# Revit family: Maxlogic sirène,flasheur,Sirène avec flasheur (Haute IP)
name_source: partatom
category: Fire Alarm Devices
units: mm (PartAtom-declared; Revit-internal decimal feet)

## family parameters
Cut with Voids When Loaded = No
Host = Face
Maintain Annotation Orientation = Yes
OmniClass Number = 23.85.30.21
OmniClass Title = Environmental Detection/Registration
Part Type = Normal
Room Calculation Point = No
Round Connector Dimension = Use Diameter
Shared = No

## types (18) — shared parameters
Adresse ligne 1 = Şerifali Mahallesi Kutup Sokak No:27/1-2-4 Ümraniye TR-34775 İSTANBUL
Durée de la garantie Travail = 2
Durée de la garantie réservé = 2
Hauteur Nominale = 95 mm
Longeur Nominale = 95 mm
Manuel d'installation = https://mavilielektronik.com
Manufacturer = Mavili Elektronik Ticaret A.Ş.
Model = Maxlogic
Numèro de Fax = (+)90 216 466 45 10
Surface de Montage = Montage à Mur
Tempèrature de Fonctionnement = (-25°C) - (+70°C)
URL = https://www.mavili.com.tr
Voltage de fonctionnement (default) = 24 V/DC
zero-valued in all types: Cost, Default Elevation

## per-type parameters (varying)
| type | Charger adresse d'appareil | Code de  Performance | Code de Produit | Couleur | Description | Deuxime Matèriel | Flasheur | Flasheur,Sirène avec Flash Profond | Hauteur de Montage | IP 33 base | IP 65 base | Largeur Nominale | Matériel Principe | Poids | Sirène Plafond | Unité de durée de garantie | protection de Classe | voltage fonction d'opération |
| Maxlogic Sirène Conventionnelle, Impermèableı(IP33) |  | EN 54-3 | ML-2440 | Rouge | Sirène Conventionnelle | Plastique | No | No | Hauteur  2,4 m du sol | Yes | No | 82 mm | Plastique Rouge PC/ABS | 154 | Yes | Ans | IP 33 | 21-28V/DC |
| Maxlogic Flasheur Conventionnelle , Impermèable(IP33) |  | EN 54-23 | ML-2450 | Rouge | Flasheur Conventionnelle | Plastique | Yes | Yes | Hauteur 2,4 m du sol | Yes | No | 82 mm | Plastique Rouge PC/ABS | 149 gr | No | Ans | IP 33 | 21-28V/DC |
| Maxlogic Sirène avec Flash Conventionnelle, Impermèableı(IP33) |  | EN 54-3 / EN 54-23 | ML-2460 | Rouge | Sirène avec flash Conventionnelle | Plastique | Yes | Yes | Hauteur 2,4 m du sol | Yes | No | 82 mm | Plastique Rouge PC/ABS | 166 gr | No | Ans | IP 33 | 21-28V/DC |
| Maxlogic Sirène Conventionnelle, Impermèable(IP65) |  | EN 54-3 | ML-2470 | Rouge | Sirène Conventionnelle | Plastique | No | No | Hauteur  2,4 m du sol | No | Yes | 100 mm | Plastique Rouge PC/ABS | 173 gr | Yes | Ans | IP 65 | 21-28V/DC |
| Maxlogic Flasheur Conventionnelle, Impermèable(IP65) |  | EN 54-23 | ML-2480 | Rouge | Flasheur Conventionnelle | Plastique | Yes | Yes | Hauteur 2,4 m du sol | No | Yes | 107 mm | Plastique Rouge PC/ABS | 168 gr | No | Ans | IP 65 | 21-28V/DC |
| Maxlogic Sirène avec flasheur Conventionnelle ,Impermèable(IP65) |  | EN 54-3 / EN 54-23 | ML-2490 | Rouge | Sirène Flasheur Conventionnelle | Plastique | Yes | Yes | Hauteur 2,4 m du sol | No | Yes | 107 mm | Plastique Rouge PC/ABS | 185 gr | No | Ans | IP 65 | 21-28V/DC |
| Maxlogic Sirène Système adressable intelligent, Impermèable (IP33) | Appareil d'adressage à main | EN 54-3 | ML-1440 | Rouge | Sirène Système Adressable Intelligent | Plastique | No | No | Hauteur 2,4 m du sol | Yes | No | 82 mm | Plastique Rouge PC/ABS | 159 gr | Yes | Ans | IP 33 | 18-33V/DC |
| Maxlogic Sirène Système Adressable Intelligent,Impermèable (IP33),Isolateur de Court-Circuit | Appareil d'adressage à main | EN 54-3 | ML-1440.SCI | Kırmızı | Sirène Système Adressable Intelligent,Isolateur de Court-Circuit | Plastique | No | No | Hauteur 2,4 m du sol | Yes | No | 82 mm | Plastique Rouge PC/ABS | 159 gr | Yes | Year | IP 33 | 18-33V/DC |
| Maxlogic Flasheur Adressable Inteligent, Impermèable(IP33) | Appareil d'adressage à main | EN 54-23 | ML-1450 | Rouge | Flasheur adressable intelligent | Plastique | Yes | Yes | Hauteur  2,4 m du sol | Yes | No | 82 mm | Plastique Rouge PC/ABS | 153 gr | No | Ans | IP 33 | 18-33V/DC |
| Maxlogic Système Flasheur Adressable Inteligent, Impermèable(IP33),Isolateur de Court-Circuit | Appareil d'adressage à main | EN 54-23 | ML-1450.SCI | Rouge | Système Flasheur Adressable Inteligent,Isolateur de Court-Circuit | Plastique | Yes | Yes | Hauteur  2,4 m du sol | Yes | No | 82 mm | Plastique Rouge PC/ABS | 153 gr | No | Ans | IP 33 | 18-33V/DC |
| Maxlogic  Sirène avec Flasheur Adressable Système Intelligent,Impermèable (IP33) | Appareil d'adressage à Main | EN 54-3 / EN 54-23 | ML-1460 | Rouge | Sirène avec Flasheur Adressable Système Intelligent | Plastique Rouge | Yes | Yes | Hauteur 2,4 m du sol | Yes | No | 82 mm | Red Plastic PC/ABS | 169 gr | No | Ans | IP 33 | 18-33V/DC |
| Maxlogic Sirène avec Flasheur Adressable Système Intelligent (IP33),Isolateur de Court-Circuit | Appareil d'adressage à Main | EN 54-3 / EN 54-23 | ML-1460.SCI | Rouge | Sirène avec Flasheur Adressable Système Intelligent avec Isolateur de Court-Circuit | Plastique | Yes | Yes | Hauteur 2,4 m du sol | Yes | No | 82 mm | Plastique Rouge PC/ABS | 169 gr | No | Ans | IP 33 | 18-33V/DC |
| Maxlogic Sirène Systeme Adressable Intelligent, Impermèable(IP65) | Appareil d'adressage à Main | EN 54-3 | ML-1470 | Rouge | Sirène Système Adressable Intelligent | Plastique | No | No | Hauteur 2,4 m du sol | No | Yes | 82 mm | Plastique Rouge PC/ABS | 178 gr | Yes | Ans | IP 65 | 18-33V/DC |
| Maxlogic Sirène Système Adressable Intelligent,Impermèableı (IP65), Isolateur de Court-Circuit | Appareil d'adressage à Main | EN 54-3 | ML-1470.SCI | Rouge | Sirène Système Adressable Intelligent avec Isolateur de Court-Circuit | Plastique | No | No | Hauteur  2,4 m du sol | No | Yes | 82 mm | Plastique Rouge PC/ABS | 178 gr | Yes | Ans | IP 65 | 18-33V/DC |
| Maxlogic Flasheur Système Adressable Intelligent,Impermèable(IP65) | Appareil d'adressage à main | EN 54-23 | ML-1480 | Rouge | Flasheur  Système Adressable Intelligent | Plastique | Yes | Yes | Hauteur 2,4 m du sol | No | Yes | 82 mm | Plastique Rouge PC/ABS | 172 gr | No | Ans | IP 65 | 18-33V/DC |
| Maxlogic  Flasheur Système Adressable Intelligent,Impermèable,Isolateur de Court-Circuit,  (IP65), | Appareil d'adressage à main | EN 54-23 | ML-1480.SCI | Rouge | Flasheur Système Adressable Intelligent ,Isolateur de Court-Circuit | Plastique | Yes | Yes | Hauteur  2,4 m du sol | No | Yes | 82 mm | Plastique Rouge PC/ABS | 172 gr | No | Ans | IP 65 | 18-33V/DC |
| Maxlogic Sirène avec Flash Système Adressable Intelligent,Impermèable(IP65) | Appareil d'adressage à Main | EN 54-3 / EN 54-23 | ML-1490 | Rouge | Sirène avec Flash Système Adressable Intelligent | Plastique | Yes | Yes | Hauteur 2,4 m du sol | No | Yes | 82 mm | Plastique Rouge PC/ABS | 188 gr | No | Ans | IP 65 | 18-33V/DC |
| Maxlogic Sirène avec flash système adressable Intelligent,Impermèableı (IP65),Isolateur de Court-Circuit | Appareil d'adressage à main | EN 54-3 / EN 54-23 | ML-1490.SCI | Rouge | iréne avec flash Système adressable  Isolateur de Court-Circuit | Plastique | Yes | Yes | Hauteur 2,4 m du sol | No | Yes | 82 mm | Plastique Rouge PC/ABS | 188 gr | No | Ans | IP 65 | 18-33V/DC |

## geometry (parser evidence)
native form markers: Sweep x4
no freeform markers — native parametric forms only
